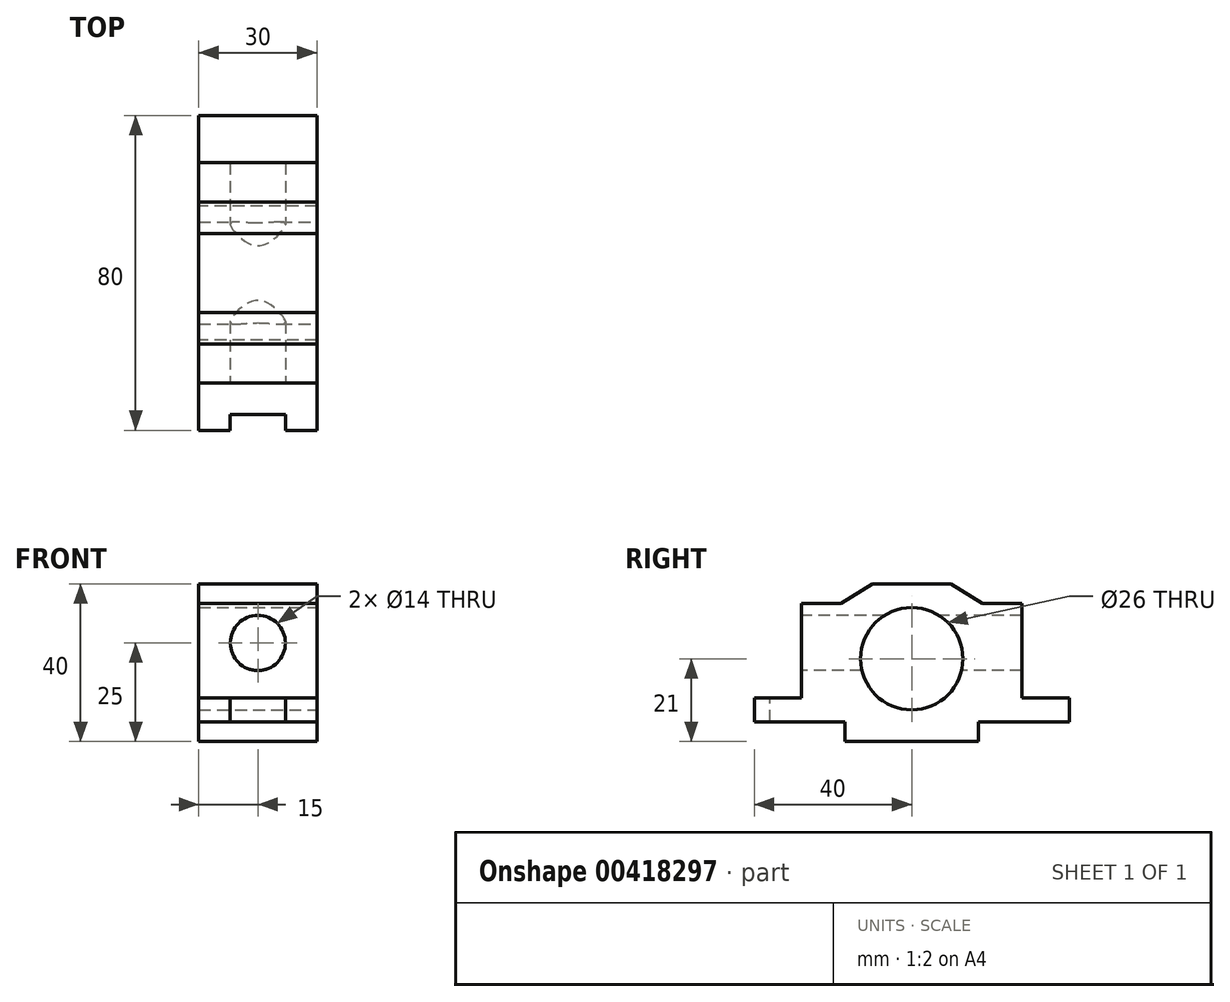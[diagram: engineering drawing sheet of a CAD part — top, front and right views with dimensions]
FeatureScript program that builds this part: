
annotation { "Feature Type Name" : "Feature", "Feature Type Description" : "" }
export const myFeature = defineFeature(function(context is Context, id is Id, definition is map)
    precondition{}
    {
        {
            var Q0;
            Q0=qCreatedBy(makeId("Right.planeOp"),FACE);
            var sketch = newSketch(context, id + "F0", { "sketchPlane" : qUnion([Q0])});
            skLineSegment(sketch, "E0", {"start": v(0, 0) * mm, "end": v(17, 0) * mm});
            skLineSegment(sketch, "E1", {"start": v(17, 0) * mm, "end": v(17, 5) * mm});
            skLineSegment(sketch, "E2", {"start": v(17, 5) * mm, "end": v(40, 5) * mm});
            skLineSegment(sketch, "E3", {"start": v(40, 5) * mm, "end": v(40, 11) * mm});
            skLineSegment(sketch, "E4", {"start": v(40, 11) * mm, "end": v(28, 11) * mm});
            skLineSegment(sketch, "E5", {"start": v(28, 11) * mm, "end": v(28, 35) * mm});
            skLineSegment(sketch, "E6", {"start": v(28, 35) * mm, "end": v(18, 35) * mm});
            skLineSegment(sketch, "E7", {"start": v(18, 35) * mm, "end": v(10, 40) * mm});
            skLineSegment(sketch, "E8", {"start": v(10, 40) * mm, "end": v(0, 40) * mm});
            skLineSegment(sketch, "E9", {"start": v(0, 40) * mm, "end": v(0, 0) * mm, "construction": true});
            skLineSegment(sketch, "E10.MirrorCS", {"start": v(-10, 40) * mm, "end": v(0, 40) * mm});
            skLineSegment(sketch, "E11.MirrorCS", {"start": v(-18, 35) * mm, "end": v(-10, 40) * mm});
            skLineSegment(sketch, "E12.MirrorCS", {"start": v(-28, 35) * mm, "end": v(-18, 35) * mm});
            skLineSegment(sketch, "E13.MirrorCS", {"start": v(-28, 11) * mm, "end": v(-28, 35) * mm});
            skLineSegment(sketch, "E14.MirrorCS", {"start": v(-40, 11) * mm, "end": v(-28, 11) * mm});
            skLineSegment(sketch, "E15.MirrorCS", {"start": v(-40, 5) * mm, "end": v(-40, 11) * mm});
            skLineSegment(sketch, "E16.MirrorCS", {"start": v(0, 0) * mm, "end": v(-17, 0) * mm});
            skLineSegment(sketch, "E17.MirrorCS", {"start": v(-17, 0) * mm, "end": v(-17, 5) * mm});
            skLineSegment(sketch, "E18.MirrorCS", {"start": v(-17, 5) * mm, "end": v(-40, 5) * mm});
            skSolve(sketch);
        }
        {
            var Q0;
            Q0 = qSketchRegion(id + "F0", true);
            extrude(context, id + "F1", {"entities" : qUnion([Q0]), "endBound" : BoundingType.SYMMETRIC, "depth" : 30 * mm});
        }
        {
            var Q0;
            Q0=makeQuery(id+"F1.opExtrude","CAP_FACE",FACE,{"disambiguationData":[OSD([sQuery(id+"F0.wireOp",EDGE,"E0"),sQuery(id+"F0.wireOp",EDGE,"E1"),sQuery(id+"F0.wireOp",EDGE,"E2"),sQuery(id+"F0.wireOp",EDGE,"E3"),sQuery(id+"F0.wireOp",EDGE,"E4"),sQuery(id+"F0.wireOp",EDGE,"E5"),sQuery(id+"F0.wireOp",EDGE,"E6"),sQuery(id+"F0.wireOp",EDGE,"E7"),sQuery(id+"F0.wireOp",EDGE,"E8"),sQuery(id+"F0.wireOp",EDGE,"E10.MirrorCS"),sQuery(id+"F0.wireOp",EDGE,"E11.MirrorCS"),sQuery(id+"F0.wireOp",EDGE,"E12.MirrorCS"),sQuery(id+"F0.wireOp",EDGE,"E13.MirrorCS"),sQuery(id+"F0.wireOp",EDGE,"E14.MirrorCS"),sQuery(id+"F0.wireOp",EDGE,"E15.MirrorCS"),sQuery(id+"F0.wireOp",EDGE,"E16.MirrorCS"),sQuery(id+"F0.wireOp",EDGE,"E17.MirrorCS"),sQuery(id+"F0.wireOp",EDGE,"E18.MirrorCS")])],"isStart":false});
            var sketch = newSketch(context, id + "F2", { "sketchPlane" : qUnion([Q0])});
            skCircle(sketch, "E19", {"center": v(0, 21) * mm, "radius": 13 * mm});
            skSolve(sketch);
        }
        {
            var Q0;
            Q0 = qSketchRegion(id + "F2", true);
            extrude(context, id + "F3", {"entities" : qUnion([Q0]), "operationType" : NewBodyOperationType.REMOVE, "endBound" : BoundingType.THROUGH_ALL, "oppositeDirection" : true, "depth" : 25 * mm});
        }
        {
            var Q0;
            Q0=makeQuery(id+"F1.opExtrude","SWEPT_FACE",FACE,{"disambiguationData":[OSD([sQuery(id+"F0.wireOp",EDGE,"E14.MirrorCS")])]});
            var sketch = newSketch(context, id + "F4", { "sketchPlane" : qUnion([Q0])});
            skLineSegment(sketch, "E20.bottom", {"start": v(-7, -36) * mm, "end": v(7, -36) * mm});
            skLineSegment(sketch, "E20.top", {"start": v(-7, -40) * mm, "end": v(7, -40) * mm});
            skLineSegment(sketch, "E20.left", {"start": v(-7, -36) * mm, "end": v(-7, -40) * mm});
            skLineSegment(sketch, "E20.right", {"start": v(7, -36) * mm, "end": v(7, -40) * mm});
            skSolve(sketch);
        }
        {
            var Q0;
            Q0 = qSketchRegion(id + "F4", true);
            extrude(context, id + "F5", {"entities" : qUnion([Q0]), "operationType" : NewBodyOperationType.REMOVE, "endBound" : BoundingType.THROUGH_ALL, "oppositeDirection" : true, "depth" : 25 * mm});
        }
        {
            var Q0;
            Q0=makeQuery(id+"F1.opExtrude","SWEPT_FACE",FACE,{"disambiguationData":[OSD([sQuery(id+"F0.wireOp",EDGE,"E13.MirrorCS")])]});
            var sketch = newSketch(context, id + "F6", { "sketchPlane" : qUnion([Q0])});
            skCircle(sketch, "E21", {"center": v(0, 25) * mm, "radius": 7 * mm});
            skSolve(sketch);
        }
        {
            var Q0;
            Q0 = qSketchRegion(id + "F6", true);
            extrude(context, id + "F7", {"entities" : qUnion([Q0]), "operationType" : NewBodyOperationType.REMOVE, "endBound" : BoundingType.THROUGH_ALL, "oppositeDirection" : true, "depth" : 25 * mm});
        }
    });
